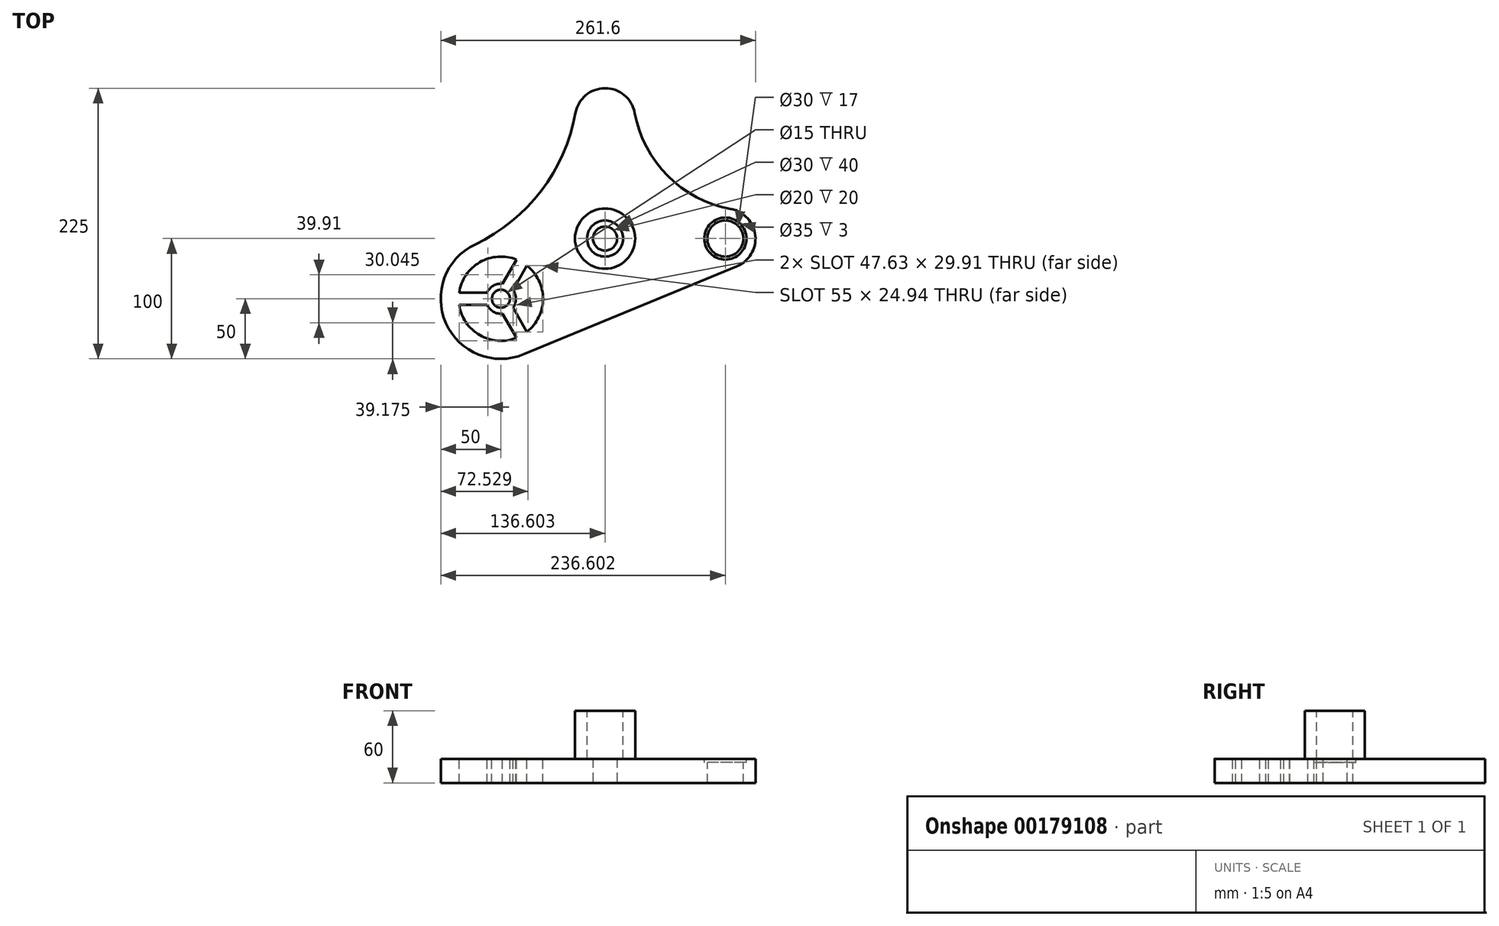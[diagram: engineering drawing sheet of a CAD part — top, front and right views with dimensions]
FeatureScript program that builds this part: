
annotation { "Feature Type Name" : "Feature", "Feature Type Description" : "" }
export const myFeature = defineFeature(function(context is Context, id is Id, definition is map)
    precondition{}
    {
        {
            var Q0;
            Q0=qCreatedBy(makeId("Top.planeOp"),FACE);
            var sketch = newSketch(context, id + "F0", { "sketchPlane" : qUnion([Q0])});
            skArc(sketch, "E0", {"start": v(-21.42, 45.18) * mm, "mid": v(-45.71, -20.26) * mm, "end": v(19.08, -46.22) * mm});
            skCircle(sketch, "E1", {"center": v(186.6, 50) * mm, "radius": 25 * mm});
            skCircle(sketch, "E2", {"center": v(86.6, 150) * mm, "radius": 17.5 * mm});
            skCircle(sketch, "E3", {"center": v(86.6, 50) * mm, "radius": 25 * mm});
            skCircle(sketch, "E4", {"center": v(0, 0) * mm, "radius": 35 * mm});
            skCircle(sketch, "E5", {"center": v(0, 0) * mm, "radius": 7.5 * mm});
            skCircle(sketch, "E6", {"center": v(0, 0) * mm, "radius": 12.5 * mm});
            skLineSegment(sketch, "E7", {"start": v(0, 0) * mm, "end": v(86.6, 50) * mm, "construction": true});
            skLineSegment(sketch, "E8", {"start": v(0, 0) * mm, "end": v(220.6, 0) * mm, "construction": true});
            skCircle(sketch, "E9", {"center": v(186.6, 50) * mm, "radius": 17.5 * mm});
            skCircle(sketch, "E10", {"center": v(86.6, 150) * mm, "radius": 25 * mm});
            skLineSegment(sketch, "E11", {"start": v(196.14, 26.9) * mm, "end": v(19.08, -46.22) * mm});
            skArc(sketch, "E12", {"start": v(111.18, 154.58) * mm, "mid": v(138.78, 102.18) * mm, "end": v(191.18, 74.58) * mm});
            skArc(sketch, "E13", {"start": v(-21.42, 45.18) * mm, "mid": v(33.53, 89.67) * mm, "end": v(62, 154.39) * mm});
            skLineSegment(sketch, "E14", {"start": v(0, 0) * mm, "end": v(3.75, -6.5) * mm, "construction": true});
            skLineSegment(sketch, "E15.0", {"start": v(10.06, -7.42) * mm, "end": v(21.65, -27.5) * mm});
            skLineSegment(sketch, "E16.trimOffspring", {"start": v(29.88, -41.76) * mm, "end": v(37.5, -54.94) * mm, "construction": true});
            skLineSegment(sketch, "E17.trimOffspring", {"start": v(6.25, -10.83) * mm, "end": v(17.5, -30.31) * mm, "construction": true});
            skLineSegment(sketch, "E18.trimOffspring", {"start": v(1.4, -12.42) * mm, "end": v(13, -32.5) * mm});
            skLineSegment(sketch, "E19.1.0", {"start": v(10.06, 7.42) * mm, "end": v(21.65, 27.5) * mm});
            skLineSegment(sketch, "E19.1.1", {"start": v(1.4, 12.42) * mm, "end": v(13, 32.5) * mm});
            skLineSegment(sketch, "E19.2.0", {"start": v(-11.46, 5) * mm, "end": v(-34.64, 5) * mm});
            skLineSegment(sketch, "E19.2.1", {"start": v(-11.46, -5) * mm, "end": v(-34.64, -5) * mm});
            skSolve(sketch);
        }
        {
            var Q0;
            {var subQ0=sQuery(id+"F0.wireOp",EDGE,"E19.1.0");Q0=makeQuery(id+"F0.imprint","IMPRINT",FACE,{"disambiguationData":[TD([[makeQuery(id+"F0.imprint","IMPRINT",EDGE,{"derivedFrom":subQ0}),1.0]])]});}
            var Q1;
            {var subQ0=sQuery(id+"F0.wireOp",EDGE,"E19.2.0");Q1=makeQuery(id+"F0.imprint","IMPRINT",FACE,{"disambiguationData":[TD([[makeQuery(id+"F0.imprint","IMPRINT",EDGE,{"derivedFrom":subQ0}),1.0]])]});}
            var Q2;
            {var subQ0=sQuery(id+"F0.wireOp",EDGE,"E15.0");Q2=makeQuery(id+"F0.imprint","IMPRINT",FACE,{"disambiguationData":[TD([[makeQuery(id+"F0.imprint","IMPRINT",EDGE,{"derivedFrom":subQ0}),-1.0]])]});}
            var Q3;
            Q3=makeQuery(id+"F0.imprint","IMPRINT",FACE,{"disambiguationData":[TD([[makeQuery(id+"F0.imprint","IMPRINT",EDGE,{"derivedFrom":sQuery(id+"F0.wireOp",EDGE,"E9")}),-1.0]])]});
            var Q4;
            Q4=makeQuery(id+"F0.imprint","IMPRINT",FACE,{"disambiguationData":[TD([[makeQuery(id+"F0.imprint","IMPRINT",EDGE,{"derivedFrom":sQuery(id+"F0.wireOp",EDGE,"E2")}),-1.0]])]});
            var Q5;
            {var subQ6=sQuery(id+"F0.wireOp",EDGE,"E0");Q5=makeQuery(id+"F0.imprint","IMPRINT",FACE,{"disambiguationData":[TD([[makeQuery(id+"F0.imprint","IMPRINT",EDGE,{"derivedFrom":subQ6}),1.0]])]});}
            var Q6;
            Q6=makeQuery(id+"F0.imprint","IMPRINT",FACE,{"disambiguationData":[TD([[makeQuery(id+"F0.imprint","IMPRINT",EDGE,{"derivedFrom":sQuery(id+"F0.wireOp",EDGE,"E5")}),-1.0]])]});
            var Q7;
            Q7=makeQuery(id+"F0.imprint","IMPRINT",FACE,{"disambiguationData":[TD([[makeQuery(id+"F0.imprint","IMPRINT",EDGE,{"derivedFrom":sQuery(id+"F0.wireOp",EDGE,"E3")}),1.0]])]});
            var Q8;
            Q8=makeQuery(id+"F0.imprint","IMPRINT",FACE,{"disambiguationData":[TD([[makeQuery(id+"F0.imprint","IMPRINT",EDGE,{"derivedFrom":sQuery(id+"F0.wireOp",EDGE,"E9")}),1.0]])]});
            var Q9;
            Q9=makeQuery(id+"F0.imprint","IMPRINT",FACE,{"disambiguationData":[TD([[makeQuery(id+"F0.imprint","IMPRINT",EDGE,{"derivedFrom":sQuery(id+"F0.wireOp",EDGE,"E2")}),1.0]])]});
            extrude(context, id + "F1", {"entities" : qUnion([Q0, Q1, Q2, Q3, Q4, Q5, Q6, Q7, Q8, Q9]), "oppositeDirection" : true, "depth" : 20 * mm});
        }
        {
            var Q0;
            Q0=makeQuery(id+"F0.imprint","IMPRINT",FACE,{"disambiguationData":[TD([[makeQuery(id+"F0.imprint","IMPRINT",EDGE,{"derivedFrom":sQuery(id+"F0.wireOp",EDGE,"E3")}),1.0]])]});
            var Q1;
            Q1=sQuery(id+"F0.wireOp",EDGE,"E3");
            extrude(context, id + "F2", {"entities" : qUnion([Q0]), "operationType" : NewBodyOperationType.ADD, "surfaceEntities" : qUnion([Q1]), "depth" : 40 * mm});
        }
        {
            var Q0;
            Q0=makeQuery(id+"F2.opExtrude","CAP_FACE",FACE,{"disambiguationData":[OSD([sQuery(id+"F0.wireOp",EDGE,"E3")])],"isStart":false});
            var sketch = newSketch(context, id + "F3", { "sketchPlane" : qUnion([Q0])});
            skCircle(sketch, "E20", {"center": v(86.6, 50) * mm, "radius": 15 * mm});
            skSolve(sketch);
        }
        {
            var Q0;
            Q0 = qSketchRegion(id + "F3", true);
            var Q1;
            Q1=makeQuery(id+"F1.opExtrude","CAP_FACE",FACE,{"disambiguationData":[OSD([sQuery(id+"F0.wireOp",EDGE,"E0"),sQuery(id+"F0.wireOp",EDGE,"E1"),sQuery(id+"F0.wireOp",EDGE,"E4"),sQuery(id+"F0.wireOp",EDGE,"E5"),sQuery(id+"F0.wireOp",EDGE,"E6"),sQuery(id+"F0.wireOp",EDGE,"E10"),sQuery(id+"F0.wireOp",EDGE,"E11"),sQuery(id+"F0.wireOp",EDGE,"E12"),sQuery(id+"F0.wireOp",EDGE,"E13"),sQuery(id+"F0.wireOp",EDGE,"E15.0"),sQuery(id+"F0.wireOp",EDGE,"E18.trimOffspring"),sQuery(id+"F0.wireOp",EDGE,"E19.1.0"),sQuery(id+"F0.wireOp",EDGE,"E19.1.1"),sQuery(id+"F0.wireOp",EDGE,"E19.2.0"),sQuery(id+"F0.wireOp",EDGE,"E19.2.1")])],"isStart":true});
            extrude(context, id + "F4", {"entities" : qUnion([Q0]), "operationType" : NewBodyOperationType.REMOVE, "endBound" : BoundingType.UP_TO_SURFACE, "oppositeDirection" : true, "endBoundEntityFace" : qUnion([Q1]), "depth" : 25 * mm});
        }
        {
            var Q0;
            Q0=makeQuery(id+"F1.opExtrude","CAP_FACE",FACE,{"disambiguationData":[OSD([sQuery(id+"F0.wireOp",EDGE,"E0"),sQuery(id+"F0.wireOp",EDGE,"E1"),sQuery(id+"F0.wireOp",EDGE,"E4"),sQuery(id+"F0.wireOp",EDGE,"E5"),sQuery(id+"F0.wireOp",EDGE,"E6"),sQuery(id+"F0.wireOp",EDGE,"E10"),sQuery(id+"F0.wireOp",EDGE,"E11"),sQuery(id+"F0.wireOp",EDGE,"E12"),sQuery(id+"F0.wireOp",EDGE,"E13"),sQuery(id+"F0.wireOp",EDGE,"E15.0"),sQuery(id+"F0.wireOp",EDGE,"E18.trimOffspring"),sQuery(id+"F0.wireOp",EDGE,"E19.1.0"),sQuery(id+"F0.wireOp",EDGE,"E19.1.1"),sQuery(id+"F0.wireOp",EDGE,"E19.2.0"),sQuery(id+"F0.wireOp",EDGE,"E19.2.1")])],"isStart":false});
            var sketch = newSketch(context, id + "F5", { "sketchPlane" : qUnion([Q0])});
            skCircle(sketch, "E21", {"center": v(86.6, -50) * mm, "radius": 10 * mm});
            skSolve(sketch);
        }
        {
            var Q0;
            Q0 = qSketchRegion(id + "F5", true);
            extrude(context, id + "F6", {"entities" : qUnion([Q0]), "operationType" : NewBodyOperationType.REMOVE, "endBound" : BoundingType.UP_TO_NEXT, "oppositeDirection" : true, "depth" : 25 * mm});
        }
        {
            var Q0;
            Q0=makeQuery(id+"F1.opExtrude","CAP_FACE",FACE,{"disambiguationData":[OSD([sQuery(id+"F0.wireOp",EDGE,"E0"),sQuery(id+"F0.wireOp",EDGE,"E1"),sQuery(id+"F0.wireOp",EDGE,"E4"),sQuery(id+"F0.wireOp",EDGE,"E5"),sQuery(id+"F0.wireOp",EDGE,"E6"),sQuery(id+"F0.wireOp",EDGE,"E10"),sQuery(id+"F0.wireOp",EDGE,"E11"),sQuery(id+"F0.wireOp",EDGE,"E12"),sQuery(id+"F0.wireOp",EDGE,"E13"),sQuery(id+"F0.wireOp",EDGE,"E15.0"),sQuery(id+"F0.wireOp",EDGE,"E18.trimOffspring"),sQuery(id+"F0.wireOp",EDGE,"E19.1.0"),sQuery(id+"F0.wireOp",EDGE,"E19.1.1"),sQuery(id+"F0.wireOp",EDGE,"E19.2.0"),sQuery(id+"F0.wireOp",EDGE,"E19.2.1")])],"isStart":true});
            var sketch = newSketch(context, id + "F7", { "sketchPlane" : qUnion([Q0])});
            skCircle(sketch, "E22", {"center": v(186.6, 50) * mm, "radius": 15 * mm});
            skSolve(sketch);
        }
        {
            var Q0;
            Q0=makeQuery(id+"F7.imprint","IMPRINT",FACE,{"disambiguationData":[TD([[makeQuery(id+"F7.imprint","IMPRINT",EDGE,{"derivedFrom":sQuery(id+"F7.wireOp",EDGE,"E22")}),1.0]])]});
            var Q1;
            Q1=sQuery(id+"F7.wireOp",EDGE,"E22");
            extrude(context, id + "F8", {"entities" : qUnion([Q0]), "operationType" : NewBodyOperationType.REMOVE, "surfaceEntities" : qUnion([Q1]), "endBound" : BoundingType.THROUGH_ALL, "oppositeDirection" : true, "depth" : 25 * mm});
        }
        {
            var Q0;
            Q0=makeQuery(id+"F1.opExtrude","CAP_FACE",FACE,{"disambiguationData":[OSD([sQuery(id+"F0.wireOp",EDGE,"E0"),sQuery(id+"F0.wireOp",EDGE,"E1"),sQuery(id+"F0.wireOp",EDGE,"E4"),sQuery(id+"F0.wireOp",EDGE,"E5"),sQuery(id+"F0.wireOp",EDGE,"E6"),sQuery(id+"F0.wireOp",EDGE,"E10"),sQuery(id+"F0.wireOp",EDGE,"E11"),sQuery(id+"F0.wireOp",EDGE,"E12"),sQuery(id+"F0.wireOp",EDGE,"E13"),sQuery(id+"F0.wireOp",EDGE,"E15.0"),sQuery(id+"F0.wireOp",EDGE,"E18.trimOffspring"),sQuery(id+"F0.wireOp",EDGE,"E19.1.0"),sQuery(id+"F0.wireOp",EDGE,"E19.1.1"),sQuery(id+"F0.wireOp",EDGE,"E19.2.0"),sQuery(id+"F0.wireOp",EDGE,"E19.2.1")])],"isStart":true});
            var sketch = newSketch(context, id + "F9", { "sketchPlane" : qUnion([Q0])});
            skCircle(sketch, "E23", {"center": v(186.6, 50) * mm, "radius": 17.5 * mm});
            skSolve(sketch);
        }
        {
            var Q0;
            Q0 = qSketchRegion(id + "F9", true);
            extrude(context, id + "F10", {"entities" : qUnion([Q0]), "operationType" : NewBodyOperationType.REMOVE, "oppositeDirection" : true, "depth" : 3 * mm});
        }
    });
